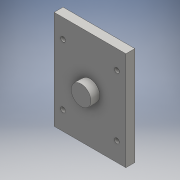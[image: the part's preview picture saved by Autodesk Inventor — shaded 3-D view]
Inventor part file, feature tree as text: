
AUTODESK INVENTOR PART (.ipt)
format: ipt  version: 2016 (Build 200138000, 138)  size: 104,960 bytes
history: native  units: mm
features: extrude x2, sketch x2
ambient origin geometry x8: Origin, YZ Plane, XZ Plane, XY Plane, X Axis, Y Axis, Z Axis, Center Point
bodies: Solid1 (feature_tree)
feature tree (4):
  extrude  "Extrusion1"  Depth=55.0mm
  extrude  "Extrusion2"  Depth=5.0mm
  sketch  "Sketch1"  dims[d0=40.0mm d1=55.0mm]
  sketch  "Sketch2"  dims[d2=2.7mm d3=2.7mm d4=2.7mm d5=2.7mm d6=5.0mm d7=0.0mm d8=11.0mm d9=5.0mm d10=0.0mm]
